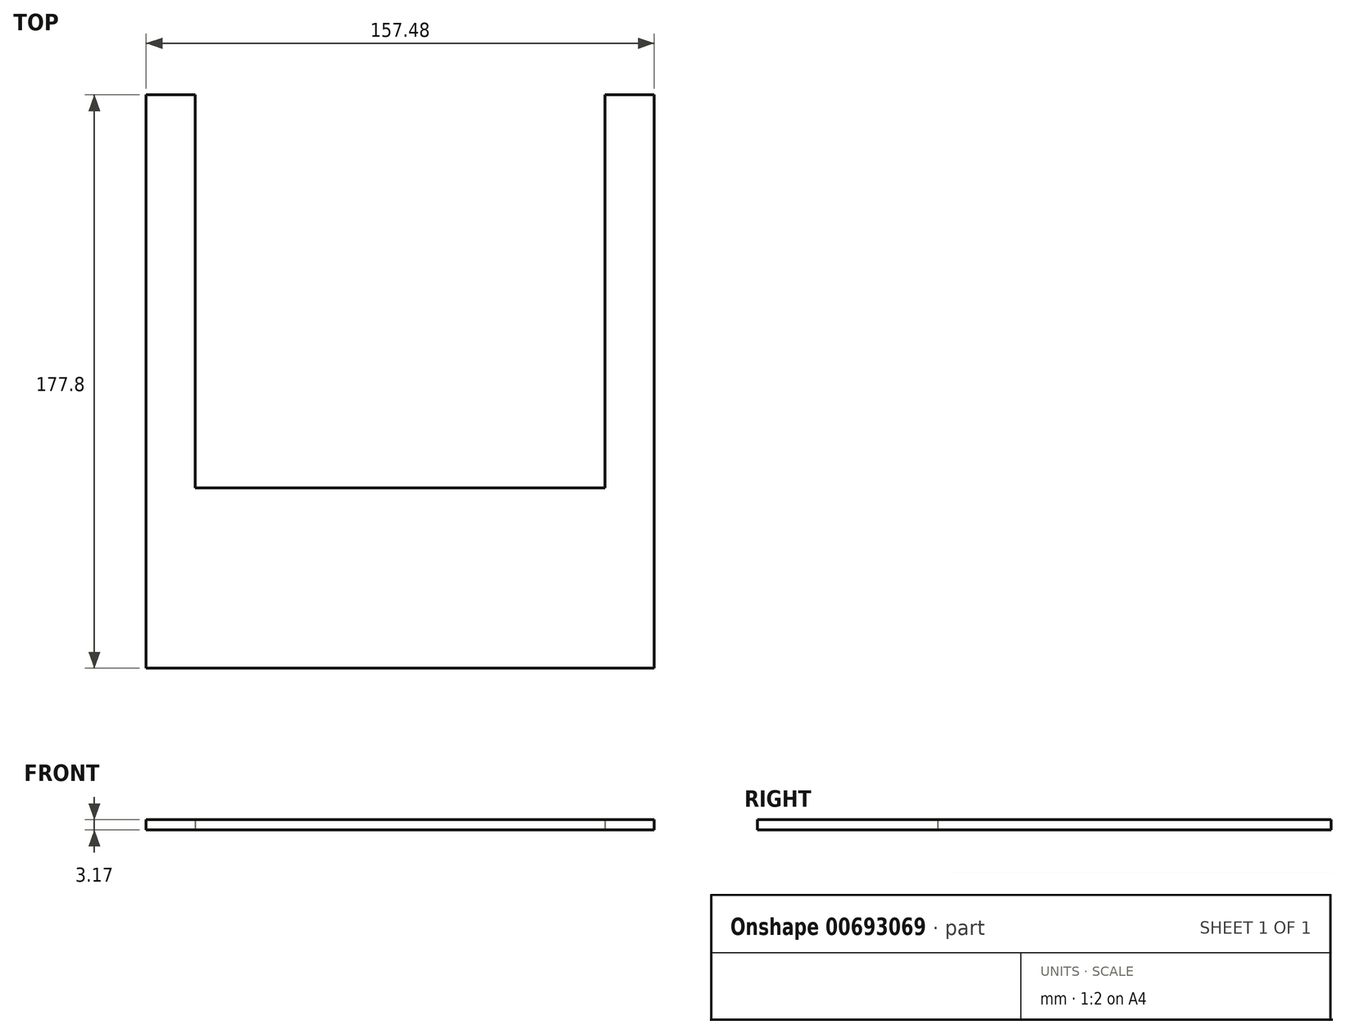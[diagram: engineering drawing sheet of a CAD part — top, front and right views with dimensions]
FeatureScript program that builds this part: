
annotation { "Feature Type Name" : "Feature", "Feature Type Description" : "" }
export const myFeature = defineFeature(function(context is Context, id is Id, definition is map)
    precondition{}
    {
        {
            var Q0;
            Q0=qCreatedBy(makeId("Top.planeOp"),FACE);
            var sketch = newSketch(context, id + "F0", { "sketchPlane" : qUnion([Q0])});
            skLineSegment(sketch, "E0.bottom", {"start": v(-80.4, 49.57) * mm, "end": v(-65.15, 49.57) * mm});
            skLineSegment(sketch, "E0.top", {"start": v(-80.4, -128.23) * mm, "end": v(77.09, -128.23) * mm});
            skLineSegment(sketch, "E0.left", {"start": v(-80.4, 49.57) * mm, "end": v(-80.4, -128.23) * mm});
            skLineSegment(sketch, "E0.right", {"start": v(77.09, 49.57) * mm, "end": v(77.09, -128.23) * mm});
            skLineSegment(sketch, "E1", {"start": v(-65.15, 49.57) * mm, "end": v(-65.15, -72.35) * mm});
            skLineSegment(sketch, "E2", {"start": v(-65.15, -72.35) * mm, "end": v(-1.65, -72.35) * mm});
            skLineSegment(sketch, "E3.trimOffspring", {"start": v(61.85, 49.57) * mm, "end": v(77.09, 49.57) * mm});
            skLineSegment(sketch, "E4.MirrorCS", {"start": v(61.85, -72.35) * mm, "end": v(-1.65, -72.35) * mm});
            skLineSegment(sketch, "E5.MirrorCS", {"start": v(61.85, 49.57) * mm, "end": v(61.85, -72.35) * mm});
            skPoint(sketch, "E6.orphan", {"position": v(-1.65, 49.57) * mm});
            skPoint(sketch, "E7.end.orphan", {"position": v(-1.65, -128.23) * mm});
            skSolve(sketch);
        }
        {
            var Q0;
            Q0=makeQuery(id+"F0.imprint","IMPRINT",FACE,{"disambiguationData":[TD([[makeQuery(id+"F0.imprint","IMPRINT",EDGE,{"derivedFrom":sQuery(id+"F0.wireOp",EDGE,"E0.top")}),1.0]])]});
            extrude(context, id + "F1", {"entities" : qUnion([Q0]), "depth" : 3.17 * mm, "offsetDistance" : 25.4 * mm});
        }
    });
